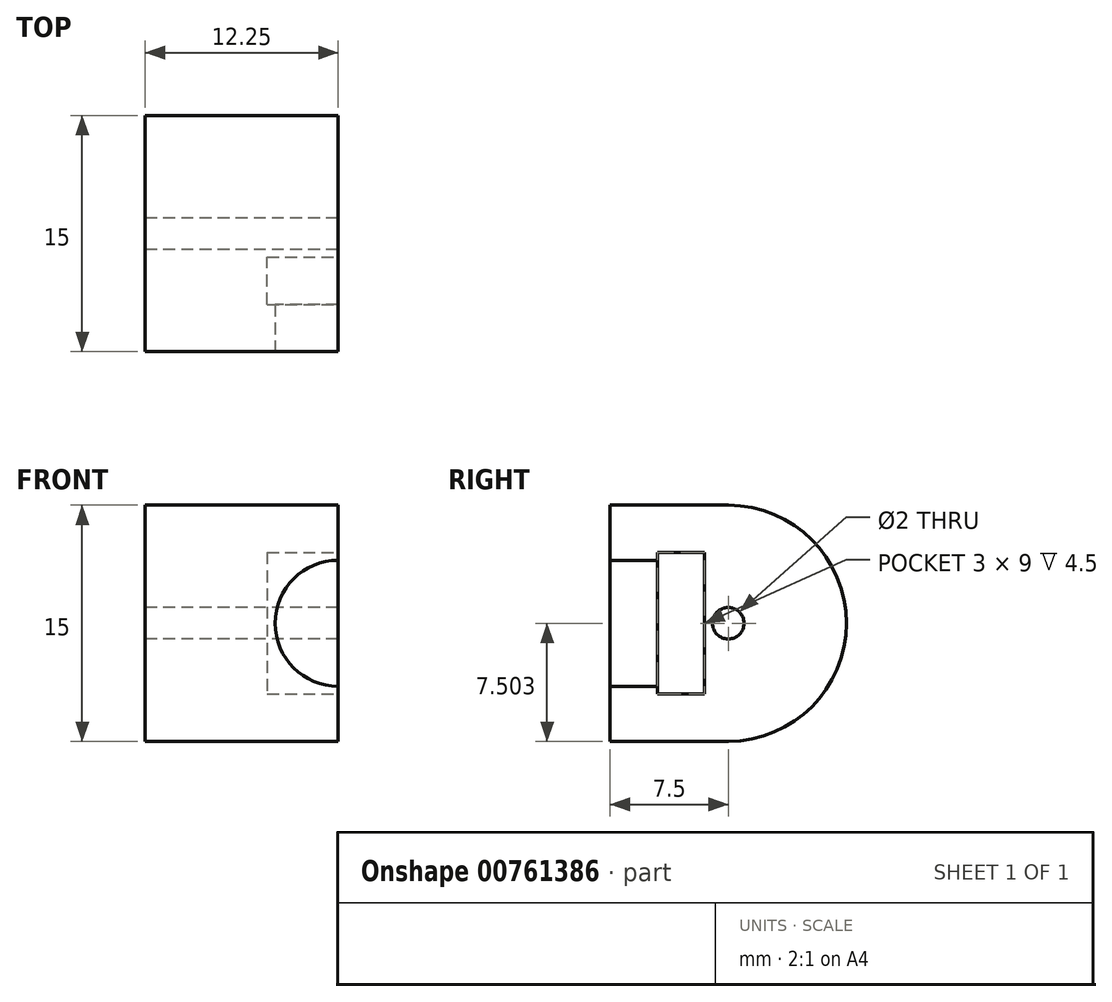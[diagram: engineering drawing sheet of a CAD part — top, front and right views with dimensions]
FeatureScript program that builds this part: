
annotation { "Feature Type Name" : "Feature", "Feature Type Description" : "" }
export const myFeature = defineFeature(function(context is Context, id is Id, definition is map)
    precondition{}
    {
        {
            var Q0;
            Q0=qCreatedBy(makeId("Front.planeOp"),FACE);
            var sketch = newSketch(context, id + "F0", { "sketchPlane" : qUnion([Q0])});
            skLineSegment(sketch, "E0.bottom", {"start": v(-39.9, 33.37) * mm, "end": v(-27.65, 33.37) * mm});
            skLineSegment(sketch, "E0.top", {"start": v(-39.9, 18.37) * mm, "end": v(-27.65, 18.37) * mm});
            skLineSegment(sketch, "E0.left", {"start": v(-39.9, 33.37) * mm, "end": v(-39.9, 18.37) * mm});
            skLineSegment(sketch, "E0.right", {"start": v(-27.65, 33.37) * mm, "end": v(-27.65, 18.37) * mm});
            skSolve(sketch);
        }
        {
            var Q0;
            Q0=makeQuery(id+"F0.imprint","IMPRINT",FACE,{"disambiguationData":[TD([[makeQuery(id+"F0.imprint","IMPRINT",EDGE,{"derivedFrom":sQuery(id+"F0.wireOp",EDGE,"E0.bottom")}),-1.0]])]});
            extrude(context, id + "F1", {"entities" : qUnion([Q0]), "depth" : 15 * mm, "offsetDistance" : 25 * mm});
        }
        {
            var Q0;
            Q0=makeQuery(id+"F1.opExtrude","CAP_EDGE",EDGE,{"disambiguationData":[OSD([sQuery(id+"F0.wireOp",EDGE,"E0.top")])],"isStart":true});
            var Q1;
            Q1=makeQuery(id+"F1.opExtrude","CAP_EDGE",EDGE,{"disambiguationData":[OSD([sQuery(id+"F0.wireOp",EDGE,"E0.bottom")])],"isStart":true});
            fillet(context, id + "F2", {"entities" : qUnion([Q0, Q1]), "radius" : (15 / 2) * mm, "tangentPropagation" : true, "allowEdgeOverflow" : false});
        }
        {
            var Q0;
            Q0=makeQuery(id+"F1.opExtrude","SWEPT_FACE",FACE,{"disambiguationData":[OSD([sQuery(id+"F0.wireOp",EDGE,"E0.left")])]});
            var sketch = newSketch(context, id + "F3", { "sketchPlane" : qUnion([Q0])});
            skCircle(sketch, "E1", {"center": v(7.5, 25.87) * mm, "radius": 1 * mm});
            skSolve(sketch);
        }
        {
            var Q0;
            Q0=makeQuery(id+"F3.imprint","IMPRINT",FACE,{"disambiguationData":[TD([[makeQuery(id+"F3.imprint","IMPRINT",EDGE,{"derivedFrom":sQuery(id+"F3.wireOp",EDGE,"E1")}),1.0]])]});
            extrude(context, id + "F4", {"entities" : qUnion([Q0]), "operationType" : NewBodyOperationType.REMOVE, "oppositeDirection" : true, "depth" : 25 * mm, "offsetDistance" : 25 * mm});
        }
        {
            var Q0;
            Q0=makeQuery(id+"F1.opExtrude","SWEPT_FACE",FACE,{"disambiguationData":[OSD([sQuery(id+"F0.wireOp",EDGE,"E0.right")])]});
            var sketch = newSketch(context, id + "F5", { "sketchPlane" : qUnion([Q0])});
            skLineSegment(sketch, "E2.bottom", {"start": v(-15, 30.37) * mm, "end": v(-9, 30.37) * mm});
            skLineSegment(sketch, "E2.top", {"start": v(-15, 21.37) * mm, "end": v(-9, 21.37) * mm});
            skLineSegment(sketch, "E2.left", {"start": v(-15, 30.37) * mm, "end": v(-15, 21.37) * mm});
            skLineSegment(sketch, "E2.right", {"start": v(-9, 30.37) * mm, "end": v(-9, 21.37) * mm});
            skLineSegment(sketch, "E3", {"start": v(-7.5, 25.87) * mm, "end": v(-9, 25.87) * mm});
            skSolve(sketch);
        }
        {
            var Q0;
            {var subQ1=sQuery(id+"F5.wireOp",EDGE,"E2.bottom");Q0=makeQuery(id+"F5.imprint","IMPRINT",FACE,{"disambiguationData":[TD([[makeQuery(id+"F5.imprint","IMPRINT",EDGE,{"derivedFrom":subQ1}),-1.0]])]});}
            extrude(context, id + "F6", {"entities" : qUnion([Q0]), "operationType" : NewBodyOperationType.REMOVE, "oppositeDirection" : true, "depth" : (9 / 2) * mm, "offsetDistance" : 25 * mm});
        }
        {
            var Q0;
            Q0=makeQuery(id+"F1.opExtrude","CAP_FACE",FACE,{"disambiguationData":[OSD([sQuery(id+"F0.wireOp",EDGE,"E0.bottom"),sQuery(id+"F0.wireOp",EDGE,"E0.top"),sQuery(id+"F0.wireOp",EDGE,"E0.left"),sQuery(id+"F0.wireOp",EDGE,"E0.right")])],"isStart":false});
            var sketch = newSketch(context, id + "F7", { "sketchPlane" : qUnion([Q0])});
            skLineSegment(sketch, "E4.bottom", {"start": v(-32.15, 30.37) * mm, "end": v(-27.65, 30.37) * mm});
            skLineSegment(sketch, "E4.top", {"start": v(-32.15, 21.37) * mm, "end": v(-27.65, 21.37) * mm});
            skLineSegment(sketch, "E4.left", {"start": v(-32.15, 30.37) * mm, "end": v(-32.15, 21.37) * mm});
            skLineSegment(sketch, "E4.right", {"start": v(-27.65, 30.37) * mm, "end": v(-27.65, 21.37) * mm});
            skCircle(sketch, "E5", {"center": v(-27.65, 25.87) * mm, "radius": 4 * mm});
            skSolve(sketch);
        }
        {
            var Q0;
            {var subQ1=sQuery(id+"F7.wireOp",EDGE,"E4.bottom");Q0=makeQuery(id+"F7.imprint","IMPRINT",FACE,{"disambiguationData":[TD([[makeQuery(id+"F7.imprint","IMPRINT",EDGE,{"derivedFrom":subQ1}),-1.0]])]});}
            extrude(context, id + "F8", {"entities" : qUnion([Q0]), "operationType" : NewBodyOperationType.ADD, "depth" : -3 * mm, "offsetDistance" : 25 * mm});
        }
    });
